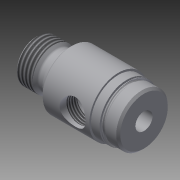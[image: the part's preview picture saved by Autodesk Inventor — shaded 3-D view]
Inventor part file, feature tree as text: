
AUTODESK INVENTOR PART (.ipt)
format: ipt  version: 2014 SP2 (Build 180246200, 246)  size: 272,896 bytes
history: native  units: in
note: dims shown in document units (in); Inventor stores cm internally (conversion verified against a paired STEP export)
features: other x119, sketch x6, revolve x5, thread x2, hole x1
ambient origin geometry x8: Origin, YZ Plane, XZ Plane, XY Plane, X Axis, Y Axis, Z Axis, Center Point
bodies: Solid1 (feature_tree)
feature tree (133):
  revolve  "Revolution1"  [1 undecoded]
  thread  "Thread1"  [1 undecoded]
  revolve  "Revolution2"  Angle=360.0deg
  hole  "Hole1"  [1 undecoded]
  revolve  "Revolution3"  [1 undecoded]
  revolve  "Revolution4"  [1 undecoded]
  thread  "Thread2"  [1 undecoded]
  revolve  "Revolution5"  [1 undecoded]
  other  "dp1_XY"
  other  "dp1_YZ"
  other  "dp1_ZX"
  other  "dp1_X"
  other  "dp1_Y"
  other  "dp1_Z"
  other  "dp1_Center"
  other  "dp2_XY"
  other  "dp2_YZ"
  other  "dp2_ZX"
  other  "dp2_X"
  other  "dp2_Y"
  other  "dp2_Z"
  other  "dp2_Center"
  other  "hh_XY"
  other  "hh_YZ"
  other  "hh_ZX"
  other  "hh_X"
  other  "hh_Y"
  other  "hh_Z"
  other  "hh_Center"
  other  "port_XY"
  other  "port_YZ"
  other  "port_ZX"
  other  "port_X"
  other  "port_Y"
  other  "port_Z"
  other  "port_Center"
  other  "rod_guide_XY"
  other  "rod_guide_YZ"
  other  "rod_guide_ZX"
  other  "rod_guide_X"
  other  "rod_guide_Y"
  other  "rod_guide_Z"
  other  "rod_guide_Center"
  other  "s1_XY"
  other  "s1_YZ"
  other  "s1_ZX"
  other  "s1_X"
  other  "s1_Y"
  other  "s1_Z"
  other  "s1_Center"
  other  "s2_XY"
  other  "s2_YZ"
  other  "s2_ZX"
  other  "s2_X"
  other  "s2_Y"
  other  "s2_Z"
  other  "s2_Center"
  other  "t1_XY"
  other  "t1_YZ"
  other  "t1_ZX"
  other  "t1_X"
  other  "t1_Y"
  other  "t1_Z"
  other  "t1_Center"
  other  "t111_XY"
  other  "t111_YZ"
  other  "t111_ZX"
  other  "t111_X"
  other  "t111_Y"
  other  "t111_Z"
  other  "t111_Center"
  other  "to_foot_bracket_XY"
  other  "to_foot_bracket_YZ"
  other  "to_foot_bracket_ZX"
  other  "to_foot_bracket_X"
  other  "to_foot_bracket_Y"
  other  "to_foot_bracket_Z"
  other  "to_foot_bracket_Center"
  other  "to_nut_XY"
  other  "to_nut_YZ"
  other  "to_nut_ZX"
  other  "to_nut_X"
  other  "to_nut_Y"
  other  "to_nut_Z"
  other  "to_nut_Center"
  other  "to_rod_XY"
  other  "to_rod_YZ"
  other  "to_rod_ZX"
  other  "to_rod_X"
  other  "to_rod_Y"
  other  "to_rod_Z"
  other  "to_rod_Center"
  other  "to_screw_XY"
  other  "to_screw_YZ"
  other  "to_screw_ZX"
  other  "to_screw_X"
  other  "to_screw_Y"
  other  "to_screw_Z"
  other  "to_screw_Center"
  other  "to_trunnion_brackets_XY"
  other  "to_trunnion_brackets_YZ"
  other  "to_trunnion_brackets_ZX"
  other  "to_trunnion_brackets_X"
  other  "to_trunnion_brackets_Y"
  other  "to_trunnion_brackets_Z"
  other  "to_trunnion_brackets_Center"
  other  "to_trunnion_brackets1_XY"
  other  "to_trunnion_brackets1_YZ"
  other  "to_trunnion_brackets1_ZX"
  other  "to_trunnion_brackets1_X"
  other  "to_trunnion_brackets1_Y"
  other  "to_trunnion_brackets1_Z"
  other  "to_trunnion_brackets1_Center"
  other  "to_trunnion_brackets2_XY"
  other  "to_trunnion_brackets2_YZ"
  other  "to_trunnion_brackets2_ZX"
  other  "to_trunnion_brackets2_X"
  other  "to_trunnion_brackets2_Y"
  other  "to_trunnion_brackets2_Z"
  other  "to_trunnion_brackets2_Center"
  other  "to_tube_XY"
  other  "to_tube_YZ"
  other  "to_tube_ZX"
  other  "to_tube_X"
  other  "to_tube_Y"
  other  "to_tube_Z"
  other  "to_tube_Center"
  sketch  "Sketch_2"  dims[d0=360.0deg d1=0.23in d2=0.0in d3=360.0deg]
  sketch  "Sketch_3"  dims[d4=0.2535in d5=0.75in d6=0.2735in d7=0.25in d8=90.0deg d9=1.594in d10=0.0in d11=360.0deg]
  sketch  "Sketch3"  dims[d12=360.0deg d13=0.1501in d14=0.0in]
  sketch  "Sketch_10"  dims[d15=360.0deg]
  sketch  "Sketch_40"  dims[d16=0.0in d17=0.0in d18=0.0in d19=0.0in d20=0.0in d21=0.0in]
  sketch  "Sketch_47"
note: 7 required parameter values undecoded (feature->parameter linkage not recoverable at this tier; creation-order binding heuristic only, values carry confidence <= 0.55)